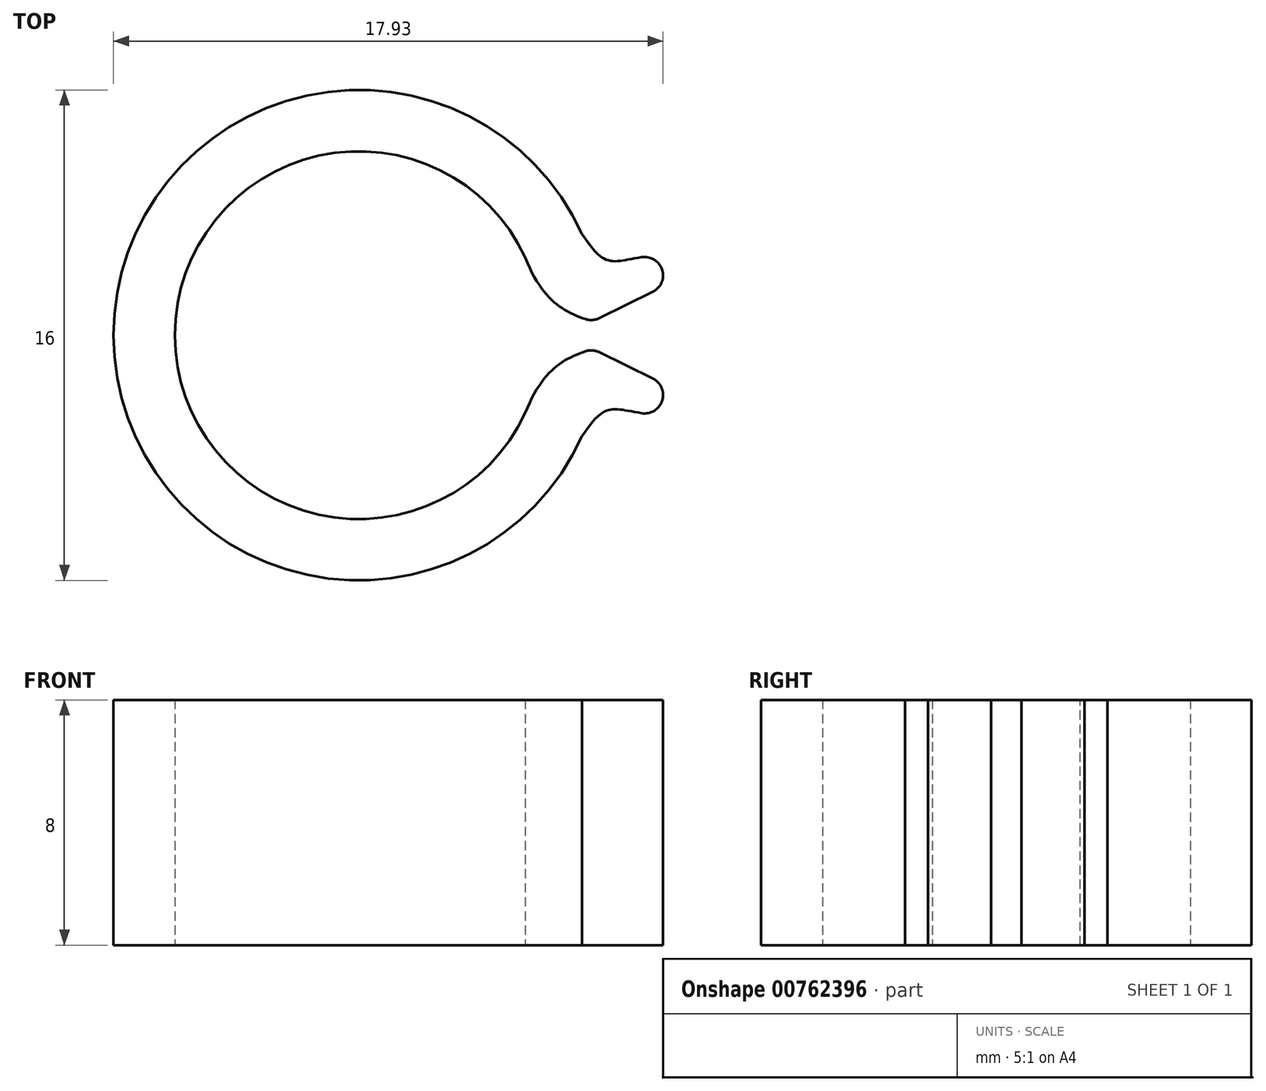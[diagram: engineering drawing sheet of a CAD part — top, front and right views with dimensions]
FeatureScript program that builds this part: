
annotation { "Feature Type Name" : "Feature", "Feature Type Description" : "" }
export const myFeature = defineFeature(function(context is Context, id is Id, definition is map)
    precondition{}
    {
        {
            var Q0;
            Q0=qCreatedBy(makeId("Top.planeOp"),FACE);
            var sketch = newSketch(context, id + "F0", { "sketchPlane" : qUnion([Q0])});
            skArc(sketch, "E0", {"start": v(5.44, 2.53) * mm, "mid": v(-1.3, 5.86) * mm, "end": v(-6, 0) * mm});
            skArc(sketch, "E1", {"start": v(7.29, 3.3) * mm, "mid": v(-1.69, 7.82) * mm, "end": v(-8, 0) * mm});
            skPoint(sketch, "E2", {"position": v(7.29, 3.3) * mm});
            skPoint(sketch, "E3", {"position": v(5.44, 2.53) * mm});
            skPoint(sketch, "E4", {"position": v(-6, 0) * mm});
            skPoint(sketch, "E5", {"position": v(-8, 0) * mm});
            skFitSpline(sketch, "E6", {"points": [v(7.29, 3.3) * mm, v(8.95, 2.5) * mm, v(12.17, 2.68) * mm], "startDerivative": vector(4.68, -7.21) * mm, "endDerivative": vector(2.33, -1.16) * mm});
            skFitSpline(sketch, "E7", {"points": [v(5.44, 2.53) * mm, v(7.16, 0.61) * mm, v(9.38, 1.3) * mm], "startDerivative": vector(2.8, -7.2) * mm, "endDerivative": vector(5.57, 6.66) * mm});
            skLineSegment(sketch, "E8", {"start": v(9.6, 1.41) * mm, "end": v(7.85, 0.56) * mm});
            skArc(sketch, "E9.filletArc", {"start": v(9.6, 1.41) * mm, "mid": v(9.9, 2.13) * mm, "end": v(9.23, 2.54) * mm});
            skArc(sketch, "E10.filletArc", {"start": v(7.4, 0.52) * mm, "mid": v(7.62, 0.5) * mm, "end": v(7.85, 0.56) * mm});
            skArc(sketch, "E11.MirrorCS", {"start": v(7.4, -0.52) * mm, "mid": v(7.62, -0.5) * mm, "end": v(7.85, -0.56) * mm});
            skArc(sketch, "E12.MirrorCS", {"start": v(9.6, -1.41) * mm, "mid": v(9.9, -2.13) * mm, "end": v(9.23, -2.54) * mm});
            skLineSegment(sketch, "E13.MirrorCS", {"start": v(9.6, -1.41) * mm, "end": v(7.85, -0.56) * mm});
            skFitSpline(sketch, "E14.MirrorCS", {"points": [v(7.29, -3.3) * mm, v(8.95, -2.5) * mm, v(12.17, -2.68) * mm], "startDerivative": vector(4.68, 7.21) * mm, "endDerivative": vector(2.33, 1.16) * mm});
            skPoint(sketch, "E15.MirrorP", {"position": v(5.44, -2.53) * mm});
            skArc(sketch, "E16.MirrorCS", {"start": v(5.44, -2.53) * mm, "mid": v(-1.3, -5.86) * mm, "end": v(-6, 0) * mm});
            skFitSpline(sketch, "E17.MirrorCS", {"points": [v(5.44, -2.53) * mm, v(7.16, -0.61) * mm, v(9.38, -1.3) * mm], "startDerivative": vector(2.8, 7.2) * mm, "endDerivative": vector(5.57, -6.66) * mm});
            skArc(sketch, "E18.MirrorCS", {"start": v(7.29, -3.3) * mm, "mid": v(-1.69, -7.82) * mm, "end": v(-8, 0) * mm});
            skPoint(sketch, "E19", {"position": v(7.83, 0.44) * mm});
            skPoint(sketch, "E20.MirrorP", {"position": v(7.83, -0.44) * mm});
            skSolve(sketch);
        }
        {
            var Q0;
            Q0=makeQuery(id+"F0.imprint","IMPRINT",FACE,{"disambiguationData":[TD([[makeQuery(id+"F0.imprint","IMPRINT",EDGE,{"derivedFrom":sQuery(id+"F0.wireOp",EDGE,"E0")}),-1.0]])]});
            extrude(context, id + "F1", {"entities" : qUnion([Q0]), "depth" : 8 * mm, "offsetDistance" : 25 * mm});
        }
    });
